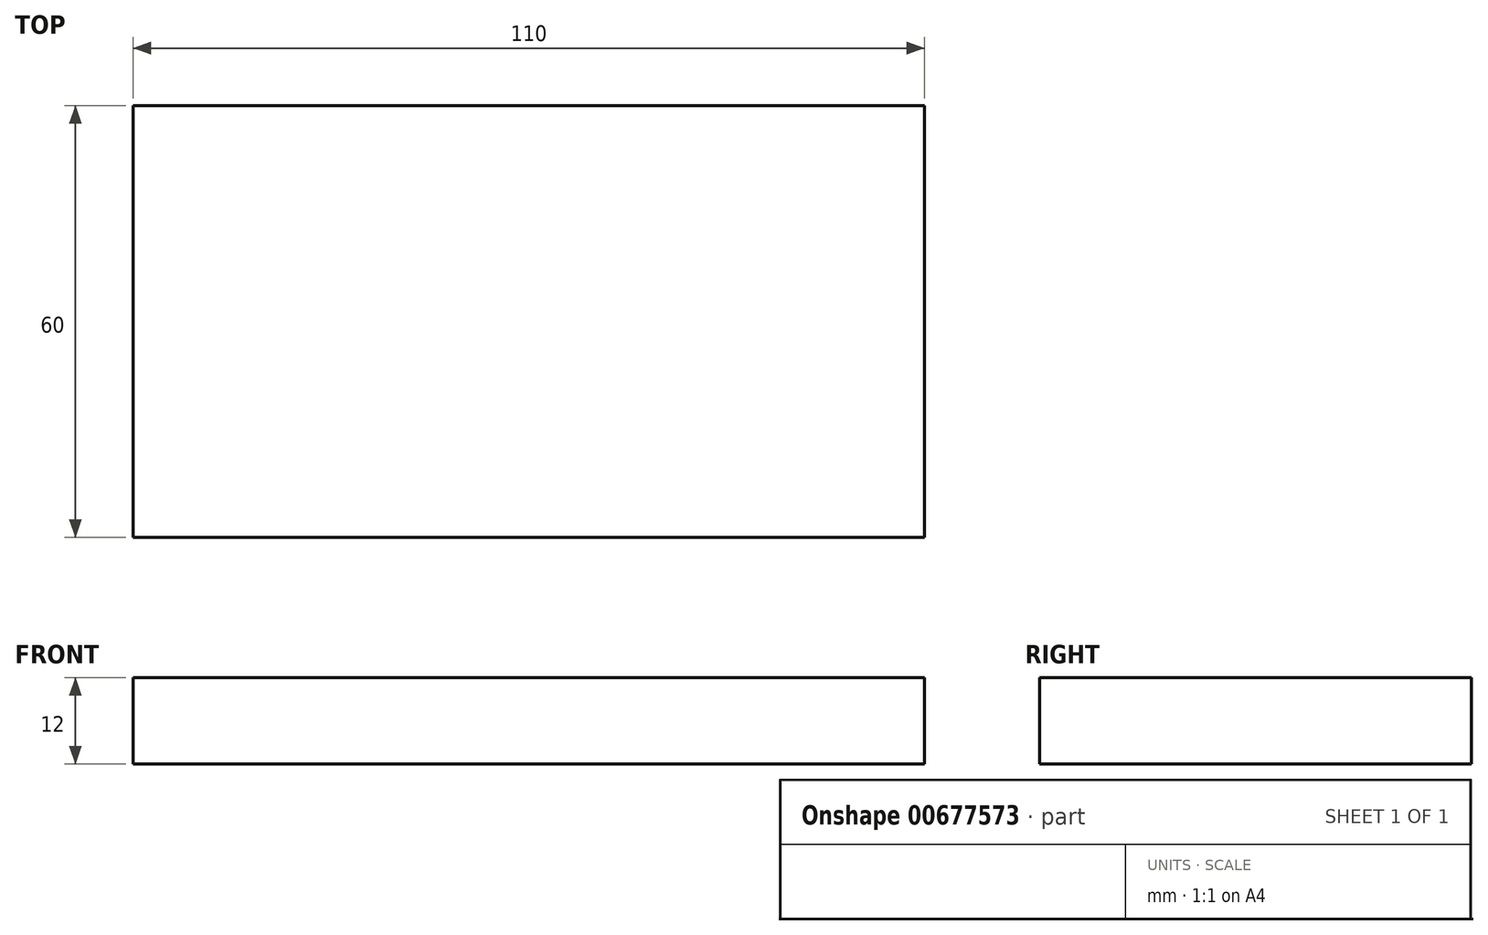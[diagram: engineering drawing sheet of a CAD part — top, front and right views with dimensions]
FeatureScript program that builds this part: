
annotation { "Feature Type Name" : "Feature", "Feature Type Description" : "" }
export const myFeature = defineFeature(function(context is Context, id is Id, definition is map)
    precondition{}
    {
        {
            var Q0;
            Q0=qCreatedBy(makeId("Top.planeOp"),FACE);
            var sketch = newSketch(context, id + "F0", { "sketchPlane" : qUnion([Q0])});
            skLineSegment(sketch, "E0.bottom", {"start": v(55, 30) * mm, "end": v(-55, 30) * mm});
            skLineSegment(sketch, "E0.top", {"start": v(55, -30) * mm, "end": v(-55, -30) * mm});
            skLineSegment(sketch, "E0.left", {"start": v(55, 30) * mm, "end": v(55, -30) * mm});
            skLineSegment(sketch, "E0.right", {"start": v(-55, 30) * mm, "end": v(-55, -30) * mm});
            skPoint(sketch, "E0.middle", {"position": v(0, 0) * mm});
            skSolve(sketch);
        }
        {
            var Q0;
            Q0=makeQuery(id+"F0.imprint","IMPRINT",FACE,{"disambiguationData":[TD([[makeQuery(id+"F0.imprint","IMPRINT",EDGE,{"derivedFrom":sQuery(id+"F0.wireOp",EDGE,"E0.bottom")}),1.0]])]});
            extrude(context, id + "F1", {"entities" : qUnion([Q0]), "depth" : 12 * mm, "offsetDistance" : 25 * mm});
        }
    });
